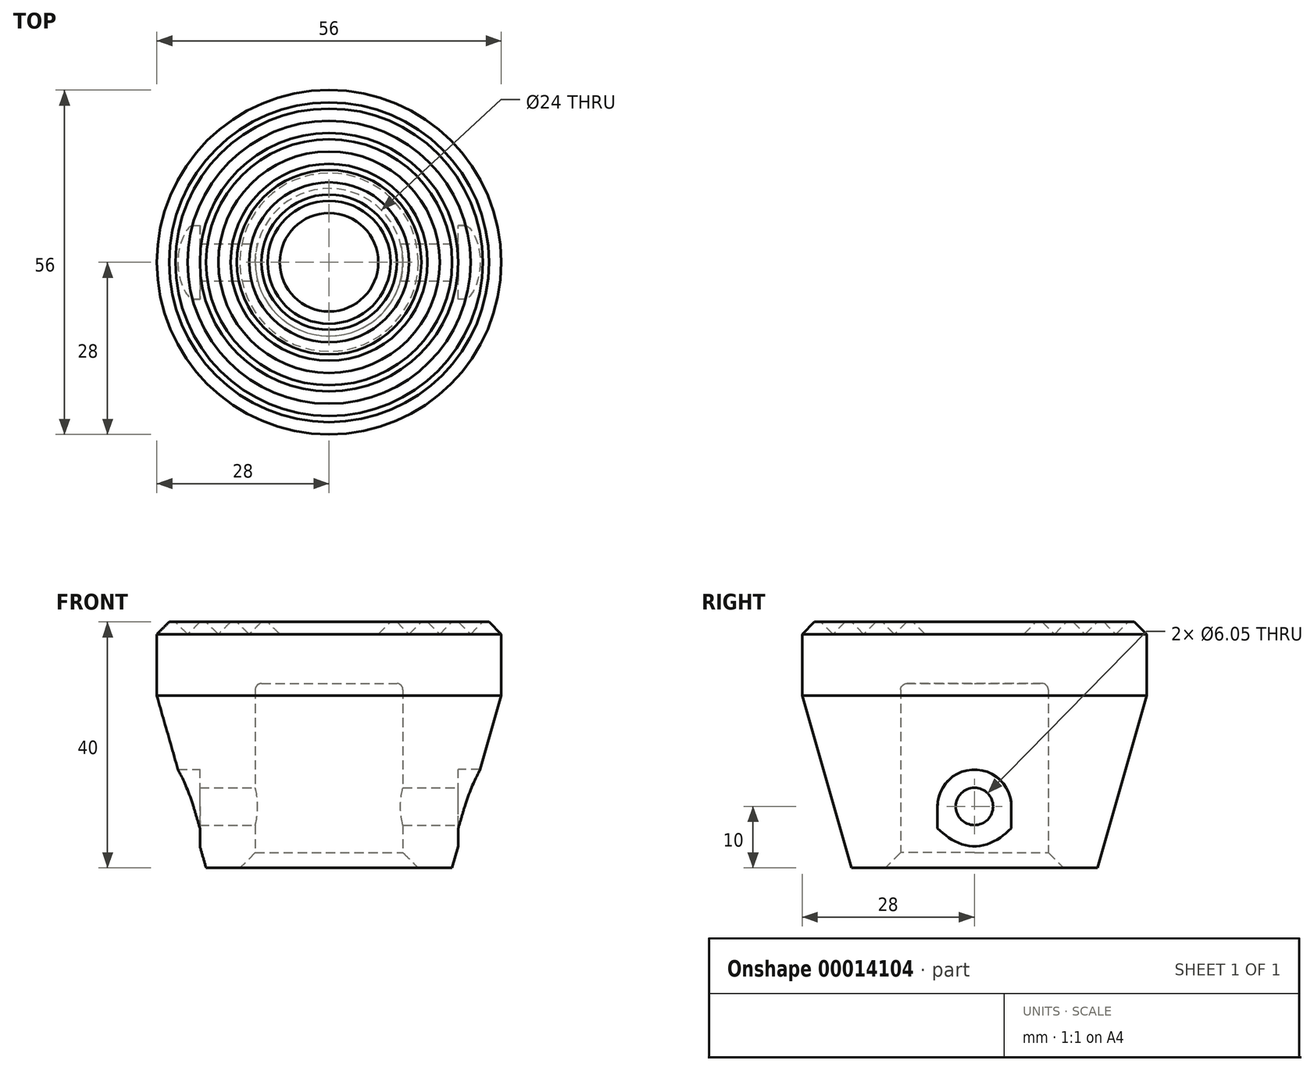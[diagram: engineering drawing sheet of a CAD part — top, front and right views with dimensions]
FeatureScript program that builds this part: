
annotation { "Feature Type Name" : "Feature", "Feature Type Description" : "" }
export const myFeature = defineFeature(function(context is Context, id is Id, definition is map)
    precondition{}
    {
        {
            var Q0;
            Q0=qCreatedBy(makeId("Front.planeOp"),FACE);
            var sketch = newSketch(context, id + "F0", { "sketchPlane" : qUnion([Q0])});
            skLineSegment(sketch, "E0", {"start": v(0, 30) * mm, "end": v(0, 38) * mm});
            skLineSegment(sketch, "E1", {"start": v(-28, 38) * mm, "end": v(-28, 28) * mm});
            skLineSegment(sketch, "E2", {"start": v(-28, 28) * mm, "end": v(-20, 0) * mm});
            skLineSegment(sketch, "E3", {"start": v(-20, 0) * mm, "end": v(-12, 0) * mm});
            skLineSegment(sketch, "E4", {"start": v(-12, 0) * mm, "end": v(-12, 29) * mm});
            skLineSegment(sketch, "E5", {"start": v(-11, 30) * mm, "end": v(0, 30) * mm});
            skPoint(sketch, "E6.visualSharp", {"position": v(-12, 30) * mm});
            skArc(sketch, "E6.filletArc", {"start": v(-11, 30) * mm, "mid": v(-11.7, 29.7) * mm, "end": v(-12, 29) * mm});
            skLineSegment(sketch, "E7", {"start": v(-28, 38) * mm, "end": v(-26, 40) * mm});
            skLineSegment(sketch, "E8", {"start": v(-25, 40) * mm, "end": v(-23, 38) * mm});
            skLineSegment(sketch, "E9", {"start": v(-23, 38) * mm, "end": v(-21, 40) * mm});
            skLineSegment(sketch, "E10", {"start": v(-20, 40) * mm, "end": v(-18, 38) * mm});
            skLineSegment(sketch, "E11", {"start": v(-18, 38) * mm, "end": v(-16, 40) * mm});
            skLineSegment(sketch, "E12", {"start": v(-15, 40) * mm, "end": v(-13, 38) * mm});
            skLineSegment(sketch, "E13", {"start": v(-13, 38) * mm, "end": v(-11, 40) * mm});
            skLineSegment(sketch, "E14", {"start": v(-10, 40) * mm, "end": v(-8, 38) * mm});
            skPoint(sketch, "E15.orphan", {"position": v(-28, 40) * mm});
            skLineSegment(sketch, "E16.trimOffspring", {"start": v(-25, 40) * mm, "end": v(-26, 40) * mm});
            skLineSegment(sketch, "E17.trimOffspring", {"start": v(-20, 40) * mm, "end": v(-21, 40) * mm});
            skLineSegment(sketch, "E18.trimOffspring", {"start": v(-15, 40) * mm, "end": v(-16, 40) * mm});
            skLineSegment(sketch, "E19.trimOffspring", {"start": v(-10, 40) * mm, "end": v(-11, 40) * mm});
            skPoint(sketch, "E20.start.orphan", {"position": v(-2, 40) * mm});
            skLineSegment(sketch, "E21", {"start": v(-8, 38) * mm, "end": v(0, 38) * mm});
            skPoint(sketch, "E22.orphan", {"position": v(0, 38.5) * mm});
            skSolve(sketch);
        }
        {
            var Q0;
            Q0=makeQuery(id+"F0.imprint","IMPRINT",FACE,{"disambiguationData":[TD([[makeQuery(id+"F0.imprint","IMPRINT",EDGE,{"derivedFrom":sQuery(id+"F0.wireOp",EDGE,"E0")}),1.0]])]});
            var Q1;
            Q1=sQuery(id+"F0.wireOp",EDGE,"E0");
            revolve(context, id + "F1", {"entities" : qUnion([Q0]), "axis" : qUnion([Q1]), "revolveType" : RevolveType.FULL});
        }
        {
            var Q0;
            Q0=makeQuery(id+"F1.opRevolve","SWEPT_EDGE",EDGE,{"disambiguationData":[OSD([sQuery(id+"F0.wireOp",EDGE,"E3"),sQuery(id+"F0.wireOp",EDGE,"E4")])]});
            chamfer(context, id + "F2", {"entities" : qUnion([Q0]), "width" : 2.5 * mm, "tangentPropagation" : true});
        }
        {
            var Q0;
            Q0=qCreatedBy(makeId("Right.planeOp"),FACE);
            cPlane(context, id + "F3", {"entities" : qUnion([Q0]), "cplaneType" : CPlaneType.OFFSET, "offset" : 21 * mm, "width" : 150 * mm, "height" : 150 * mm});
        }
        {
            var Q0;
            Q0=qCreatedBy(id+"F3.planeOp",FACE);
            var sketch = newSketch(context, id + "F4", { "sketchPlane" : qUnion([Q0])});
            skArc(sketch, "E23", {"start": v(6, 10) * mm, "mid": v(0, 16) * mm, "end": v(-6, 10) * mm});
            skLineSegment(sketch, "E24", {"start": v(-6, 10) * mm, "end": v(-6, 0) * mm});
            skLineSegment(sketch, "E25", {"start": v(-6, 0) * mm, "end": v(6, 0) * mm});
            skLineSegment(sketch, "E26", {"start": v(6, 0) * mm, "end": v(6, 10) * mm});
            skSolve(sketch);
        }
        {
            var Q0;
            Q0=makeQuery(id+"F4.imprint","IMPRINT",FACE,{"disambiguationData":[TD([[makeQuery(id+"F4.imprint","IMPRINT",EDGE,{"derivedFrom":sQuery(id+"F4.wireOp",EDGE,"E23")}),1.0]])]});
            extrude(context, id + "F5", {"entities" : qUnion([Q0]), "operationType" : NewBodyOperationType.REMOVE, "depth" : 25 * mm});
        }
        {
            var Q0;
            Q0=qCreatedBy(makeId("Right.planeOp"),FACE);
            cPlane(context, id + "F6", {"entities" : qUnion([Q0]), "cplaneType" : CPlaneType.OFFSET, "offset" : 21 * mm, "oppositeDirection" : true, "width" : 150 * mm, "height" : 150 * mm});
        }
        {
            var Q0;
            Q0=qCreatedBy(id+"F6.planeOp",FACE);
            var sketch = newSketch(context, id + "F7", { "sketchPlane" : qUnion([Q0])});
            skArc(sketch, "E27.0", {"start": v(6, 10) * mm, "mid": v(0, 16) * mm, "end": v(-6, 10) * mm});
            skLineSegment(sketch, "E28", {"start": v(6, 10) * mm, "end": v(6, 0) * mm});
            skLineSegment(sketch, "E29", {"start": v(6, 0) * mm, "end": v(-6, 0) * mm});
            skLineSegment(sketch, "E30", {"start": v(-6, 0) * mm, "end": v(-6, 10) * mm});
            skSolve(sketch);
        }
        {
            var Q0;
            Q0=makeQuery(id+"F7.imprint","IMPRINT",FACE,{"disambiguationData":[TD([[makeQuery(id+"F7.imprint","IMPRINT",EDGE,{"derivedFrom":sQuery(id+"F7.wireOp",EDGE,"E27.0")}),1.0]])]});
            extrude(context, id + "F8", {"entities" : qUnion([Q0]), "operationType" : NewBodyOperationType.REMOVE, "oppositeDirection" : true, "depth" : 25 * mm});
        }
        {
            var Q0;
            Q0=makeQuery(id+"F5.boolean.opBoolean","COPY",FACE,{"derivedFrom":makeQuery(id+"F5.opExtrude","CAP_FACE",FACE,{"disambiguationData":[OSD([sQuery(id+"F4.wireOp",EDGE,"E23"),sQuery(id+"F4.wireOp",EDGE,"E24"),sQuery(id+"F4.wireOp",EDGE,"E25"),sQuery(id+"F4.wireOp",EDGE,"E26")])],"isStart":true})});
            var sketch = newSketch(context, id + "F9", { "sketchPlane" : qUnion([Q0])});
            skArc(sketch, "E31.0", {"start": v(6, 10) * mm, "mid": v(0, 16) * mm, "end": v(-6, 10) * mm});
            skCircle(sketch, "E32", {"center": v(0, 10) * mm, "radius": 3.03 * mm});
            skSolve(sketch);
        }
        {
            var Q0;
            Q0=makeQuery(id+"F9.imprint","IMPRINT",FACE,{"disambiguationData":[TD([[makeQuery(id+"F9.imprint","IMPRINT",EDGE,{"derivedFrom":sQuery(id+"F9.wireOp",EDGE,"E32")}),1.0]])]});
            extrude(context, id + "F10", {"entities" : qUnion([Q0]), "operationType" : NewBodyOperationType.REMOVE, "endBound" : BoundingType.THROUGH_ALL, "oppositeDirection" : true, "depth" : 25 * mm});
        }
    });
